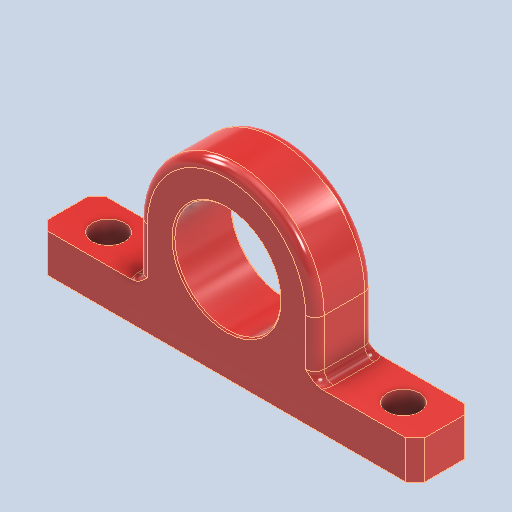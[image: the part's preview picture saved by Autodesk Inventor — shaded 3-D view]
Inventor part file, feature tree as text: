
AUTODESK INVENTOR PART (.ipt)
format: ipt  version: 2023 (Build 270158000, 158)  size: 181,760 bytes
history: native  units: in
note: dims shown in document units (in); Inventor stores cm internally (conversion verified against a paired STEP export)
features: hole x1
ambient origin geometry x8: Origin, YZ Plane, XZ Plane, XY Plane, X Axis, Y Axis, Z Axis, Center Point
bodies: Solid1 (feature_tree)
feature tree (1):
  hole  "Hole Cut"  [1 undecoded]
note: 1 required parameter value undecoded (feature->parameter linkage not recoverable at this tier; creation-order binding heuristic only, values carry confidence <= 0.55)
